# Revit family: QF_Kelvinator_738260_KCHMT48.18_2-Door_Mega_Top_Prep_48_Long
name_source: partatom
category: Specialty Equipment
units: mm (PartAtom-declared; Revit-internal decimal feet)

## family parameters
Always vertical = Yes
Cut with Voids When Loaded = No
Part Type = Normal
Room Calculation Point = No
Round Connector Dimension = Use Diameter
Shared = No
Work Plane-Based = No

## types (1)
- QF_Kelvinator_738260_KCHMT48.18_2-Door_Mega_Top_Prep_48_Long
    Apparent Power = 0 VA
    Conn Conduit = Yes
    Conn Plug = 5-15P
    Cycle = 60 Hz
    Default Elevation = 0 "
    Depth = 35.433 "
    Description = 2-Door Mega Top Prep 48" Long
    Elec Conn Connection Height = 0 "
    Elec Conn RI Height = 0 "
    FL Amps = 4 A
    Foodservice Equipment Identifier = Yes
    HP = 1/3
    Height = 43.307 "
    Identify Quantity as Lot = Yes
    Item Number = 738260
    Length = 48.228 "
    Manufacturer = Kelvinator Commercial
    Max Overcurrent Protection = 0 A
    Min Ckt Ampacity = 0 A
    Model = 738260 (KCHMT48.18)
    Number of Poles = 1
    Phase = 1
    Refrigerant Type = R290
    Volts = 115 V
    Watts = 700 W
    Weight in Pounds = 227.076

## geometry (parser evidence)
native form markers: Sweep x7
no freeform markers — native parametric forms only
